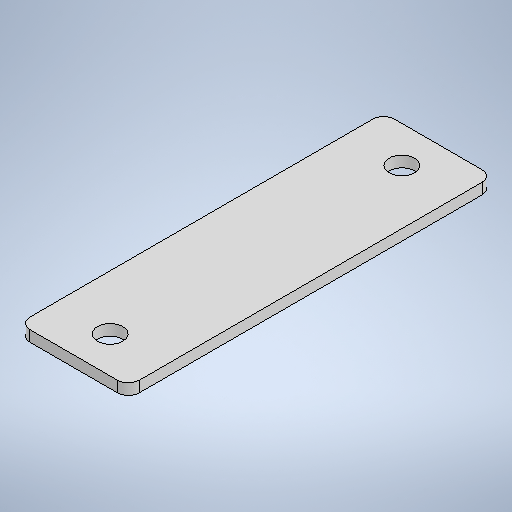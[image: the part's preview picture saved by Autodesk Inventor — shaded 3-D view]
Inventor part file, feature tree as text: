
AUTODESK INVENTOR PART (.ipt)
format: ipt  version: 2025 (Build 290162010, 162A)  size: 284,160 bytes
history: native  units: mm
features: sheet_metal_op x1, chamfer x1, sketch x1, other x1
ambient origin geometry x8: Origin, YZ Plane, XZ Plane, XY Plane, X Axis, Y Axis, Z Axis, Center Point
bodies: Body1 (feature_tree)
feature tree (4):
  sheet_metal_op  "Face3"
  chamfer  "Corner Round1"
  sketch  "Sketch1"  dims[d61=500.0mm d154=60.0mm d155=200.0mm d156=6.0mm d157=20.0mm d159=14.0mm d160=6.0mm]
  other  "Plate5"
